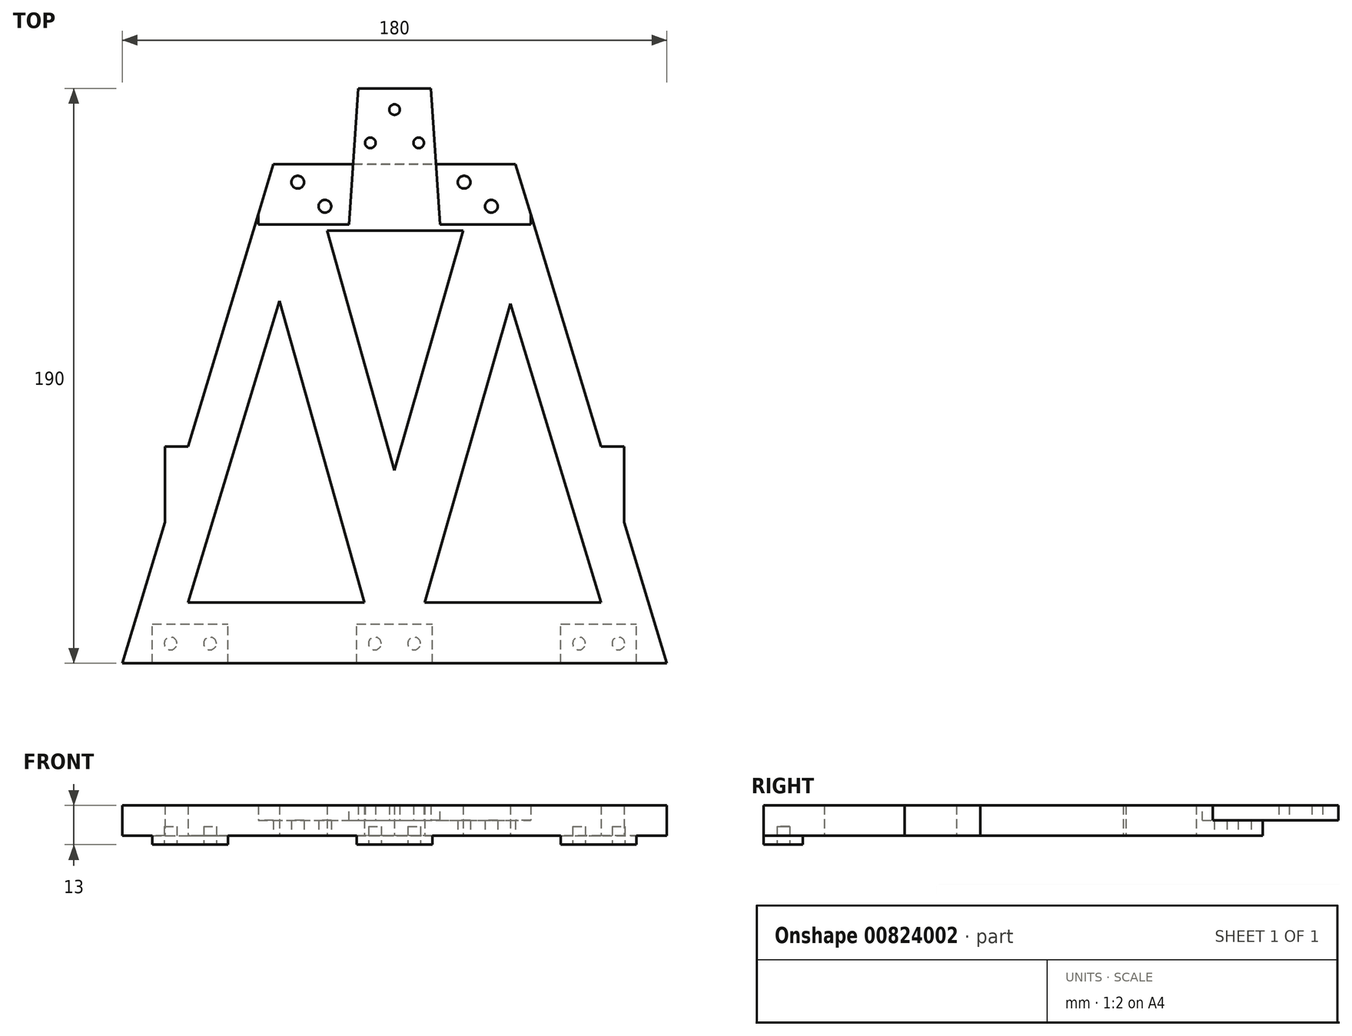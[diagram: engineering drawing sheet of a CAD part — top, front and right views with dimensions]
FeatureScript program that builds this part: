
annotation { "Feature Type Name" : "Feature", "Feature Type Description" : "" }
export const myFeature = defineFeature(function(context is Context, id is Id, definition is map)
    precondition{}
    {
        {
            var Q0;
            Q0=qCreatedBy(makeId("Top.planeOp"),FACE);
            var sketch = newSketch(context, id + "F0", { "sketchPlane" : qUnion([Q0])});
            skLineSegment(sketch, "E0.bottom", {"start": v(-15, 12.5) * mm, "end": v(15, 12.5) * mm});
            skLineSegment(sketch, "E0.left", {"start": v(-15, 12.5) * mm, "end": v(-15, -12.5) * mm});
            skLineSegment(sketch, "E0.right", {"start": v(15, 12.5) * mm, "end": v(15, -12.5) * mm});
            skLineSegment(sketch, "E1", {"start": v(-15, -12.5) * mm, "end": v(-40, -12.5) * mm});
            skLineSegment(sketch, "E2", {"start": v(15, -12.5) * mm, "end": v(40, -12.5) * mm});
            skLineSegment(sketch, "E3", {"start": v(-40, -12.5) * mm, "end": v(-68.3, -105.86) * mm});
            skLineSegment(sketch, "E4", {"start": v(-90, -177.5) * mm, "end": v(90, -177.5) * mm});
            skLineSegment(sketch, "E5", {"start": v(90, -177.5) * mm, "end": v(75.87, -130.86) * mm});
            skLineSegment(sketch, "E6", {"start": v(-22.28, -34.46) * mm, "end": v(22.72, -34.46) * mm});
            skLineSegment(sketch, "E7", {"start": v(22.72, -34.46) * mm, "end": v(0, -113.74) * mm});
            skLineSegment(sketch, "E8", {"start": v(0, -113.74) * mm, "end": v(-22.28, -34.46) * mm});
            skLineSegment(sketch, "E9", {"start": v(-68.27, -157.5) * mm, "end": v(-10, -157.5) * mm});
            skLineSegment(sketch, "E10", {"start": v(-10, -157.5) * mm, "end": v(-38.04, -57.74) * mm});
            skLineSegment(sketch, "E11", {"start": v(-38.04, -57.74) * mm, "end": v(-68.27, -157.5) * mm});
            skLineSegment(sketch, "E12", {"start": v(10, -157.5) * mm, "end": v(68.27, -157.5) * mm});
            skLineSegment(sketch, "E13", {"start": v(68.27, -157.5) * mm, "end": v(38.32, -58.68) * mm});
            skLineSegment(sketch, "E14", {"start": v(38.32, -58.68) * mm, "end": v(10, -157.5) * mm});
            skLineSegment(sketch, "E15", {"start": v(-75.87, -130.86) * mm, "end": v(-75.87, -105.86) * mm});
            skLineSegment(sketch, "E16", {"start": v(-75.87, -105.86) * mm, "end": v(-68.3, -105.86) * mm});
            skLineSegment(sketch, "E17", {"start": v(75.87, -130.86) * mm, "end": v(75.87, -105.86) * mm});
            skLineSegment(sketch, "E18", {"start": v(75.87, -105.86) * mm, "end": v(68.3, -105.86) * mm});
            skLineSegment(sketch, "E19.trimOffspring", {"start": v(68.3, -105.86) * mm, "end": v(40, -12.5) * mm});
            skLineSegment(sketch, "E20.trimOffspring", {"start": v(-75.87, -130.86) * mm, "end": v(-90, -177.5) * mm});
            skSolve(sketch);
        }
        {
            var Q0;
            Q0 = qSketchRegion(id + "F0", true);
            extrude(context, id + "F1", {"entities" : qUnion([Q0]), "depth" : 10 * mm, "offsetDistance" : 25 * mm});
        }
        {
            var Q0;
            Q0=makeQuery(id+"F1.opExtrude","CAP_FACE",FACE,{"disambiguationData":[OSD([sQuery(id+"F0.wireOp",EDGE,"E0.bottom"),sQuery(id+"F0.wireOp",EDGE,"E0.left"),sQuery(id+"F0.wireOp",EDGE,"E0.right"),sQuery(id+"F0.wireOp",EDGE,"E1"),sQuery(id+"F0.wireOp",EDGE,"E2"),sQuery(id+"F0.wireOp",EDGE,"E3"),sQuery(id+"F0.wireOp",EDGE,"E4"),sQuery(id+"F0.wireOp",EDGE,"E5"),sQuery(id+"F0.wireOp",EDGE,"E6"),sQuery(id+"F0.wireOp",EDGE,"E7"),sQuery(id+"F0.wireOp",EDGE,"E8"),sQuery(id+"F0.wireOp",EDGE,"E9"),sQuery(id+"F0.wireOp",EDGE,"E10"),sQuery(id+"F0.wireOp",EDGE,"E11"),sQuery(id+"F0.wireOp",EDGE,"E12"),sQuery(id+"F0.wireOp",EDGE,"E13"),sQuery(id+"F0.wireOp",EDGE,"E14"),sQuery(id+"F0.wireOp",EDGE,"E15"),sQuery(id+"F0.wireOp",EDGE,"E16"),sQuery(id+"F0.wireOp",EDGE,"E17"),sQuery(id+"F0.wireOp",EDGE,"E18"),sQuery(id+"F0.wireOp",EDGE,"E19.trimOffspring"),sQuery(id+"F0.wireOp",EDGE,"E20.trimOffspring")])],"isStart":true});
            var sketch = newSketch(context, id + "F2", { "sketchPlane" : qUnion([Q0])});
            skLineSegment(sketch, "E21.bottom", {"start": v(-15, 12.5) * mm, "end": v(15, 12.5) * mm});
            skLineSegment(sketch, "E21.top", {"start": v(-15, -12.5) * mm, "end": v(15, -12.5) * mm});
            skLineSegment(sketch, "E21.left", {"start": v(-15, 12.5) * mm, "end": v(-15, -12.5) * mm});
            skLineSegment(sketch, "E21.right", {"start": v(15, 12.5) * mm, "end": v(15, -12.5) * mm});
            skSolve(sketch);
        }
        {
            var Q0;
            Q0 = qSketchRegion(id + "F2", true);
            extrude(context, id + "F3", {"entities" : qUnion([Q0]), "operationType" : NewBodyOperationType.REMOVE, "oppositeDirection" : true, "depth" : 5 * mm, "offsetDistance" : 25 * mm});
        }
        {
            var Q0;
            Q0=makeQuery(id+"F1.opExtrude","CAP_FACE",FACE,{"disambiguationData":[OSD([sQuery(id+"F0.wireOp",EDGE,"E0.bottom"),sQuery(id+"F0.wireOp",EDGE,"E0.left"),sQuery(id+"F0.wireOp",EDGE,"E0.right"),sQuery(id+"F0.wireOp",EDGE,"E1"),sQuery(id+"F0.wireOp",EDGE,"E2"),sQuery(id+"F0.wireOp",EDGE,"E3"),sQuery(id+"F0.wireOp",EDGE,"E4"),sQuery(id+"F0.wireOp",EDGE,"E5"),sQuery(id+"F0.wireOp",EDGE,"E6"),sQuery(id+"F0.wireOp",EDGE,"E7"),sQuery(id+"F0.wireOp",EDGE,"E8"),sQuery(id+"F0.wireOp",EDGE,"E9"),sQuery(id+"F0.wireOp",EDGE,"E10"),sQuery(id+"F0.wireOp",EDGE,"E11"),sQuery(id+"F0.wireOp",EDGE,"E12"),sQuery(id+"F0.wireOp",EDGE,"E13"),sQuery(id+"F0.wireOp",EDGE,"E14"),sQuery(id+"F0.wireOp",EDGE,"E15"),sQuery(id+"F0.wireOp",EDGE,"E16"),sQuery(id+"F0.wireOp",EDGE,"E17"),sQuery(id+"F0.wireOp",EDGE,"E18"),sQuery(id+"F0.wireOp",EDGE,"E19.trimOffspring"),sQuery(id+"F0.wireOp",EDGE,"E20.trimOffspring")])],"isStart":false});
            var sketch = newSketch(context, id + "F4", { "sketchPlane" : qUnion([Q0])});
            skLineSegment(sketch, "E22.bottom", {"start": v(-45, -12.5) * mm, "end": v(-15, -12.5) * mm});
            skLineSegment(sketch, "E22.top", {"start": v(-45, -32.5) * mm, "end": v(-15, -32.5) * mm});
            skLineSegment(sketch, "E22.left", {"start": v(-45, -12.5) * mm, "end": v(-45, -32.5) * mm});
            skLineSegment(sketch, "E22.right", {"start": v(-15, -12.5) * mm, "end": v(-15, -32.5) * mm});
            skLineSegment(sketch, "E23.bottom", {"start": v(15, -12.5) * mm, "end": v(45, -12.5) * mm});
            skLineSegment(sketch, "E23.top", {"start": v(15, -32.5) * mm, "end": v(45, -32.5) * mm});
            skLineSegment(sketch, "E23.left", {"start": v(15, -12.5) * mm, "end": v(15, -32.5) * mm});
            skLineSegment(sketch, "E23.right", {"start": v(45, -12.5) * mm, "end": v(45, -32.5) * mm});
            skSolve(sketch);
        }
        {
            var Q0;
            Q0 = qSketchRegion(id + "F4", true);
            extrude(context, id + "F5", {"entities" : qUnion([Q0]), "operationType" : NewBodyOperationType.REMOVE, "oppositeDirection" : true, "depth" : 5 * mm, "offsetDistance" : 25 * mm});
        }
        {
            var Q0;
            Q0=makeQuery(id+"F1.opExtrude","CAP_FACE",FACE,{"disambiguationData":[OSD([sQuery(id+"F0.wireOp",EDGE,"E0.bottom"),sQuery(id+"F0.wireOp",EDGE,"E0.left"),sQuery(id+"F0.wireOp",EDGE,"E0.right"),sQuery(id+"F0.wireOp",EDGE,"E1"),sQuery(id+"F0.wireOp",EDGE,"E2"),sQuery(id+"F0.wireOp",EDGE,"E3"),sQuery(id+"F0.wireOp",EDGE,"E4"),sQuery(id+"F0.wireOp",EDGE,"E5"),sQuery(id+"F0.wireOp",EDGE,"E6"),sQuery(id+"F0.wireOp",EDGE,"E7"),sQuery(id+"F0.wireOp",EDGE,"E8"),sQuery(id+"F0.wireOp",EDGE,"E9"),sQuery(id+"F0.wireOp",EDGE,"E10"),sQuery(id+"F0.wireOp",EDGE,"E11"),sQuery(id+"F0.wireOp",EDGE,"E12"),sQuery(id+"F0.wireOp",EDGE,"E13"),sQuery(id+"F0.wireOp",EDGE,"E14"),sQuery(id+"F0.wireOp",EDGE,"E15"),sQuery(id+"F0.wireOp",EDGE,"E16"),sQuery(id+"F0.wireOp",EDGE,"E17"),sQuery(id+"F0.wireOp",EDGE,"E18"),sQuery(id+"F0.wireOp",EDGE,"E19.trimOffspring"),sQuery(id+"F0.wireOp",EDGE,"E20.trimOffspring")])],"isStart":false});
            var sketch = newSketch(context, id + "F6", { "sketchPlane" : qUnion([Q0])});
            skLineSegment(sketch, "E24.bottom", {"start": v(-80, -177.5) * mm, "end": v(-55, -177.5) * mm});
            skLineSegment(sketch, "E24.top", {"start": v(-80, -164.5) * mm, "end": v(-55, -164.5) * mm});
            skLineSegment(sketch, "E24.left", {"start": v(-80, -177.5) * mm, "end": v(-80, -164.5) * mm});
            skLineSegment(sketch, "E24.right", {"start": v(-55, -177.5) * mm, "end": v(-55, -164.5) * mm});
            skLineSegment(sketch, "E25.bottom", {"start": v(-12.5, -177.5) * mm, "end": v(12.5, -177.5) * mm});
            skLineSegment(sketch, "E25.top", {"start": v(-12.5, -164.5) * mm, "end": v(12.5, -164.5) * mm});
            skLineSegment(sketch, "E25.left", {"start": v(-12.5, -177.5) * mm, "end": v(-12.5, -164.5) * mm});
            skLineSegment(sketch, "E25.right", {"start": v(12.5, -177.5) * mm, "end": v(12.5, -164.5) * mm});
            skLineSegment(sketch, "E26.bottom", {"start": v(55, -177.5) * mm, "end": v(80, -177.5) * mm});
            skLineSegment(sketch, "E26.top", {"start": v(55, -164.5) * mm, "end": v(80, -164.5) * mm});
            skLineSegment(sketch, "E26.left", {"start": v(55, -177.5) * mm, "end": v(55, -164.5) * mm});
            skLineSegment(sketch, "E26.right", {"start": v(80, -177.5) * mm, "end": v(80, -164.5) * mm});
            skSolve(sketch);
        }
        {
            var Q0;
            Q0 = qSketchRegion(id + "F6", true);
            extrude(context, id + "F7", {"entities" : qUnion([Q0]), "operationType" : NewBodyOperationType.ADD, "oppositeDirection" : true, "depth" : 13 * mm, "offsetDistance" : 25 * mm});
        }
        {
            var Q0;
            Q0=makeQuery(id+"F7.opExtrude","CAP_FACE",FACE,{"disambiguationData":[OSD([sQuery(id+"F6.wireOp",EDGE,"E24.bottom"),sQuery(id+"F6.wireOp",EDGE,"E24.top"),sQuery(id+"F6.wireOp",EDGE,"E24.left"),sQuery(id+"F6.wireOp",EDGE,"E24.right")])],"isStart":false});
            var sketch = newSketch(context, id + "F8", { "sketchPlane" : qUnion([Q0])});
            skCircle(sketch, "E27", {"center": v(-74, 171) * mm, "radius": 2.1 * mm});
            skCircle(sketch, "E28", {"center": v(-61, 171) * mm, "radius": 2.1 * mm});
            skCircle(sketch, "E29", {"center": v(-6.5, 171) * mm, "radius": 2.1 * mm});
            skPoint(sketch, "E29.centerSnap0", {"position": v(-55, 171) * mm});
            skCircle(sketch, "E30", {"center": v(6.5, 171) * mm, "radius": 2.1 * mm});
            skCircle(sketch, "E31", {"center": v(61, 171) * mm, "radius": 2.1 * mm});
            skCircle(sketch, "E32", {"center": v(74, 171) * mm, "radius": 2.1 * mm});
            skSolve(sketch);
        }
        {
            var Q0;
            Q0 = qSketchRegion(id + "F8", true);
            extrude(context, id + "F9", {"entities" : qUnion([Q0]), "operationType" : NewBodyOperationType.REMOVE, "oppositeDirection" : true, "depth" : 6 * mm, "offsetDistance" : 25 * mm});
        }
        {
            var Q0;
            Q0=makeQuery(id+"F3.boolean.opBoolean","COPY",FACE,{"derivedFrom":makeQuery(id+"F3.opExtrude","CAP_FACE",FACE,{"disambiguationData":[OSD([sQuery(id+"F2.wireOp",EDGE,"E21.bottom"),sQuery(id+"F2.wireOp",EDGE,"E21.top"),sQuery(id+"F2.wireOp",EDGE,"E21.left"),sQuery(id+"F2.wireOp",EDGE,"E21.right")])],"isStart":false})});
            var sketch = newSketch(context, id + "F10", { "sketchPlane" : qUnion([Q0])});
            skLineSegment(sketch, "E33", {"start": v(-15, -12.5) * mm, "end": v(-15, 32.5) * mm});
            skLineSegment(sketch, "E34", {"start": v(-15, 32.5) * mm, "end": v(-12, -12.5) * mm});
            skLineSegment(sketch, "E35", {"start": v(-12, -12.5) * mm, "end": v(-15, -12.5) * mm});
            skLineSegment(sketch, "E36", {"start": v(15, -12.5) * mm, "end": v(15, 32.5) * mm});
            skLineSegment(sketch, "E37", {"start": v(15, 32.5) * mm, "end": v(12, -12.5) * mm});
            skLineSegment(sketch, "E38", {"start": v(12, -12.5) * mm, "end": v(15, -12.5) * mm});
            skSolve(sketch);
        }
        {
            var Q0;
            Q0 = qSketchRegion(id + "F10", true);
            extrude(context, id + "F11", {"entities" : qUnion([Q0]), "operationType" : NewBodyOperationType.REMOVE, "oppositeDirection" : true, "depth" : 25 * mm, "offsetDistance" : 25 * mm});
        }
        {
            var Q0;
            Q0=makeQuery(id+"F1.opExtrude","CAP_FACE",FACE,{"disambiguationData":[OSD([sQuery(id+"F0.wireOp",EDGE,"E0.bottom"),sQuery(id+"F0.wireOp",EDGE,"E0.left"),sQuery(id+"F0.wireOp",EDGE,"E0.right"),sQuery(id+"F0.wireOp",EDGE,"E1"),sQuery(id+"F0.wireOp",EDGE,"E2"),sQuery(id+"F0.wireOp",EDGE,"E3"),sQuery(id+"F0.wireOp",EDGE,"E4"),sQuery(id+"F0.wireOp",EDGE,"E5"),sQuery(id+"F0.wireOp",EDGE,"E6"),sQuery(id+"F0.wireOp",EDGE,"E7"),sQuery(id+"F0.wireOp",EDGE,"E8"),sQuery(id+"F0.wireOp",EDGE,"E9"),sQuery(id+"F0.wireOp",EDGE,"E10"),sQuery(id+"F0.wireOp",EDGE,"E11"),sQuery(id+"F0.wireOp",EDGE,"E12"),sQuery(id+"F0.wireOp",EDGE,"E13"),sQuery(id+"F0.wireOp",EDGE,"E14"),sQuery(id+"F0.wireOp",EDGE,"E15"),sQuery(id+"F0.wireOp",EDGE,"E16"),sQuery(id+"F0.wireOp",EDGE,"E17"),sQuery(id+"F0.wireOp",EDGE,"E18"),sQuery(id+"F0.wireOp",EDGE,"E19.trimOffspring"),sQuery(id+"F0.wireOp",EDGE,"E20.trimOffspring")])],"isStart":true});
            var sketch = newSketch(context, id + "F12", { "sketchPlane" : qUnion([Q0])});
            skCircle(sketch, "E39", {"center": v(0, -5.5) * mm, "radius": 1.75 * mm});
            skCircle(sketch, "E40", {"center": v(-8, 5.5) * mm, "radius": 1.75 * mm});
            skCircle(sketch, "E41", {"center": v(8, 5.5) * mm, "radius": 1.75 * mm});
            skCircle(sketch, "E42", {"center": v(32, 26.46) * mm, "radius": 2.1 * mm});
            skCircle(sketch, "E43", {"center": v(23, 18.5) * mm, "radius": 2.1 * mm});
            skCircle(sketch, "E44", {"center": v(-23, 26.46) * mm, "radius": 2.1 * mm});
            skCircle(sketch, "E45", {"center": v(-32, 18.5) * mm, "radius": 2.1 * mm});
            skSolve(sketch);
        }
        {
            var Q0;
            Q0 = qSketchRegion(id + "F12", true);
            extrude(context, id + "F13", {"entities" : qUnion([Q0]), "operationType" : NewBodyOperationType.REMOVE, "oppositeDirection" : true, "depth" : 25 * mm, "offsetDistance" : 25 * mm});
        }
    });
